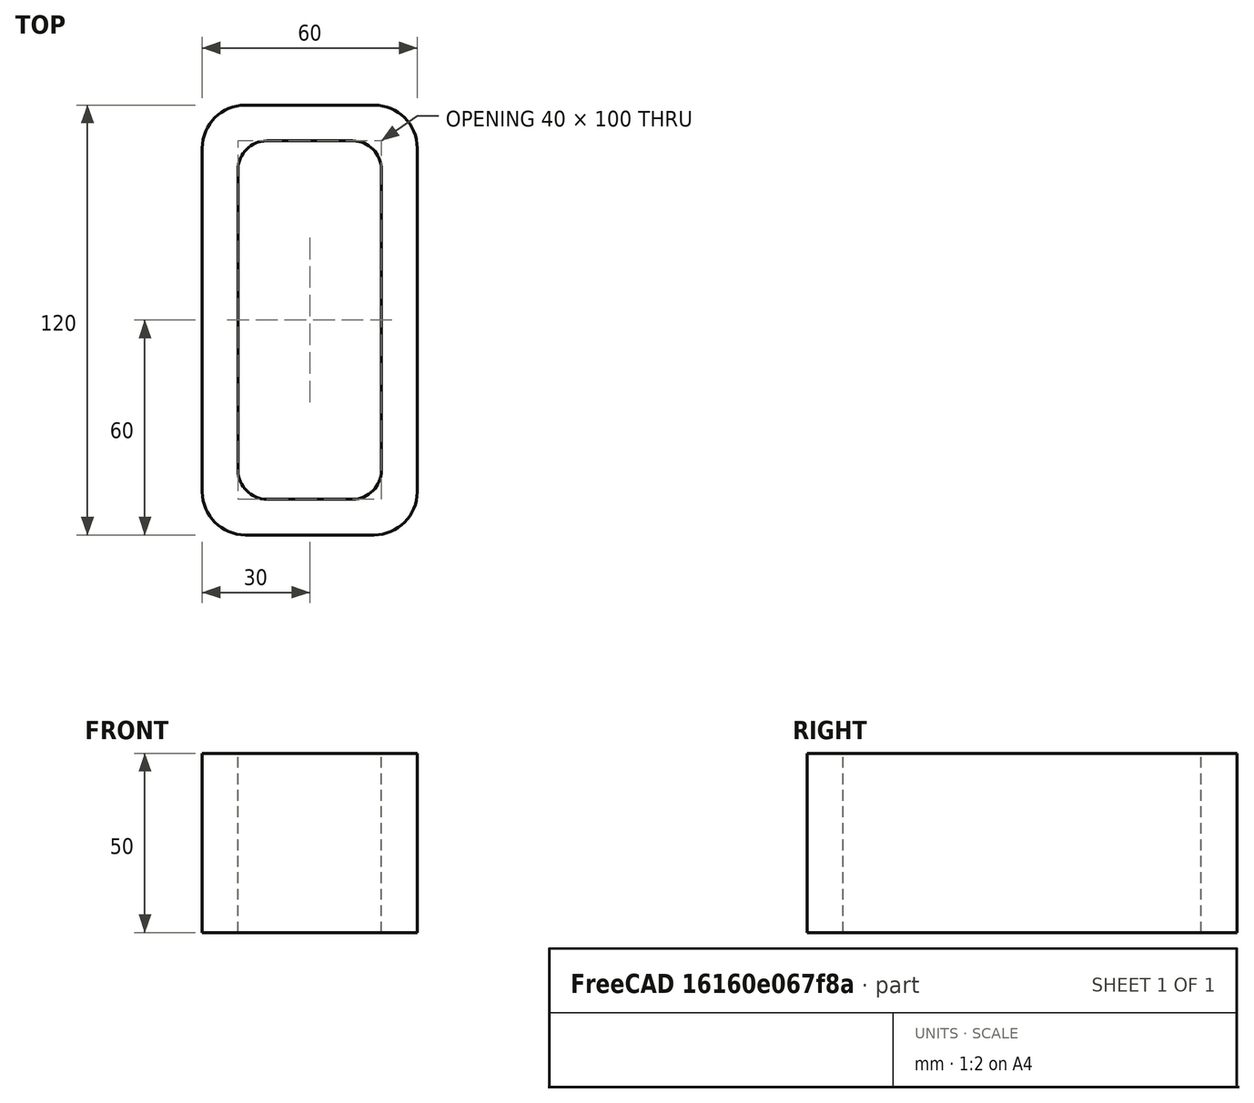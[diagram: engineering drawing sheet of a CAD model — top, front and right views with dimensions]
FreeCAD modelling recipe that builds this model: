
FCSTD DOCUMENT  (FreeCAD 0.15R4671 (Git))
Label: Rectangular hollow section 120x60x10 EN10219 S235JRH
License: All rights reserved
LicenseURL: http://en.wikipedia.org/wiki/All_rights_reserved
objects: Sketcher::SketchObject×1, Part::Extrusion×1
note: 2 computed .brp shape members not serialized (recipe doc carries the construction recipe); baked Part::Feature solids carry a one-line shape summary decoded from their .brp

FEATURE [Sketcher::SketchObject] Sketch
  sketch-geometry (16):
    g0: LineSegment StartX=-12 StartY=50 StartZ=0 EndX=12 EndY=50 EndZ=0
    g1: LineSegment StartX=20 StartY=42 StartZ=0 EndX=20 EndY=-42 EndZ=0
    g2: LineSegment StartX=12 StartY=-50 StartZ=0 EndX=-12 EndY=-50 EndZ=0
    g3: LineSegment StartX=-20 StartY=-42 StartZ=0 EndX=-20 EndY=42 EndZ=0
    g4: LineSegment StartX=-18 StartY=60 StartZ=0 EndX=18 EndY=60 EndZ=0
    g5: LineSegment StartX=30 StartY=48 StartZ=0 EndX=30 EndY=-48 EndZ=0
    g6: LineSegment StartX=18 StartY=-60 StartZ=0 EndX=-18 EndY=-60 EndZ=0
    g7: LineSegment StartX=-30 StartY=-48 StartZ=0 EndX=-30 EndY=48 EndZ=0
    g8: ArcOfCircle CenterX=-12 CenterY=42 CenterZ=0 NormalX=0 NormalY=0 NormalZ=1 Radius=8 StartAngle=1.5708 EndAngle=3.14159
    g9: ArcOfCircle CenterX=12 CenterY=42 CenterZ=0 NormalX=0 NormalY=0 NormalZ=1 Radius=8 StartAngle=0 EndAngle=1.5708
    g10: ArcOfCircle CenterX=12 CenterY=-42 CenterZ=0 NormalX=0 NormalY=0 NormalZ=1 Radius=8 StartAngle=4.71239 EndAngle=6.28319
    g11: ArcOfCircle CenterX=-12 CenterY=-42 CenterZ=0 NormalX=0 NormalY=0 NormalZ=1 Radius=8 StartAngle=3.14159 EndAngle=4.71239
    g12: ArcOfCircle CenterX=18 CenterY=48 CenterZ=0 NormalX=0 NormalY=0 NormalZ=1 Radius=12 StartAngle=0 EndAngle=1.5708
    g13: ArcOfCircle CenterX=18 CenterY=-48 CenterZ=0 NormalX=0 NormalY=0 NormalZ=1 Radius=12 StartAngle=4.71239 EndAngle=6.28319
    g14: ArcOfCircle CenterX=-18 CenterY=-48 CenterZ=0 NormalX=0 NormalY=0 NormalZ=1 Radius=12 StartAngle=3.14159 EndAngle=4.71239
    g15: ArcOfCircle CenterX=-18 CenterY=48 CenterZ=0 NormalX=0 NormalY=0 NormalZ=1 Radius=12 StartAngle=1.5708 EndAngle=3.14159
  constraints (36):
    c: Horizontal(g2)
    c: Vertical(g3)
    c: Horizontal(g6)
    c: Vertical(g7)
    c: Tangent(g3,g8) = 1.5708
    c: Tangent(g0,g8) = 1.5708
    c: Tangent(g0,g9) = 1.5708
    c: Tangent(g1,g9) = 1.5708
    c: Tangent(g1,g10) = 1.5708
    c: Tangent(g2,g10) = 1.5708
    c: Tangent(g2,g11) = 1.5708
    c: Tangent(g3,g11) = 1.5708
    c: Tangent(g4,g12) = 1.5708
    c: Tangent(g5,g12) = 1.5708
    c: Tangent(g5,g13) = 1.5708
    c: Tangent(g6,g13) = 1.5708
    c: Tangent(g6,g14) = 1.5708
    c: Tangent(g7,g14) = 1.5708
    c: Tangent(g7,g15) = 1.5708
    c: Tangent(g4,g15) = 1.5708
    c: Equal(g9,g8)
    c: Equal(g9,g11)
    c: Equal(g9,g10)
    c: Equal(g12,g15)
    c: Equal(g12,g14)
    c: Equal(g12,g13)
    c: Symmetric(g4,g6,g-1)
    c: Symmetric(g7,g5,g-2)
    c: DistanceY(g4,g6) = -120
    c: DistanceX(g7,g5) = 60
    c: Symmetric(g3,g1,g-2)
    c: Symmetric(g0,g2,g-1)
    c: DistanceY(g0,g4) = 10
    c: DistanceX(g5,g1) = -10
    c: Radius(g9) = 8
    c: Radius(g12) = 12
FEATURE [Part::Extrusion] Extrude  label="Rectangular hollow section 120x60x10 EN10219 S235JRH"
  Base = -> Sketch
  Dir = (0,0,50)
  Solid = true
